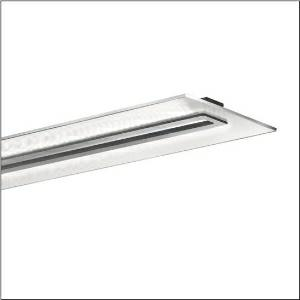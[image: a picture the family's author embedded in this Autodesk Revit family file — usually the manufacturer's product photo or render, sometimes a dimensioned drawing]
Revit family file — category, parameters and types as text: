
# Revit family: vega_r__11_5mn238dlc003_c003
name_source: partatom
category: Lighting Fixtures
units: mm (PartAtom-declared; Revit-internal decimal feet)

## family parameters
Cut with Voids When Loaded = No
Host = Face
Light Source = No
Part Type = Normal
Room Calculation Point = No
Round Connector Dimension = Use Diameter
Shared = No

## types (1)
- --- (1 x LED 3000K / CRI = 80 (unbekannt), 4300 lm, 3000K)
    Apparent Load = 35 VA
    CIE Flux Codes = 61 86 97 62 100
    Color Rendering = 80
    Color Temperature = 3000K
    Default Elevation = 1800 mm
    Description = Vega® 11, office luminaire, primary light control with prismatic reflector, of PMMA, transparent prismatic structure, CAT 2 (L<= 1500cd/m²), light emission: direct/indirect distribution, primary light characteristic: symmetric, installation type: suspended mounting, surface-mounted, LED rated luminous flux: 4.300 lm, light colour: 830, colour temperature: 3000K, control gear: ECG, with terminal, 3+2-pole, max. 2.5mm², mains connection: 230V, AC, 50Hz, connection cable inclusive, cable length: 1,5 m, rated input power: 35W, luminaire housing, rectangular, rounded, of aluminium section, anodised, metallic grey (RAL 9006), length: 1.250 mm, width: 350 mm, height: 43mm, luminaire housing, lower part, of aluminium section, anodised, metallic grey (RAL 9006), of PC, grey, protection rating (complete): IP20, insulation class (complete): insulation class I (protective earthing), certification: CE, standard: EN 50419, packaging unit: 1 piece
    Height = 40 mm  [stored 0.131234 ft]
    Lamp = 1 x LED 3000K / CRI >= 80 (unbekannt)
    Lamp Light Flux = 4300 lm
    Lamp count = 1
    Length = 1250 mm
    Luminous efficacy = 123 lm/W
    Manufacturer = Siteco
    ModVariant = No
    Model = 5MN238DLC003
    Mounting Place = Ceiling
    Mounting Type = Pendant
    Number of Poles = 1
    OnlyDefault = Yes
    Power Factor = 1
    Product Name = Vega® 11
    Product group = office luminaire | ceiling pendant
    ProductGroupID = 905
    Protection Class = Protection class I
    Protection Degree = IP 20
    RLX_Detail_Level = 1
    RlxData = <blob elided: 62757 chars, md5=ca971ff4>
    Socket = socket
    Standby Power = 0 W
    System Light Flux = 4300 lm
    System Power = 35 W
    Type Comments = factory setting: luminous flux: 100 % | dim-lin: 254 | 260 mA
    Type Image = l_1004807.jpg
    URL = http://relux.com
    VarID = @adj_147249
    Voltage = 0 V
    Weight = 0.00 kg
    Width = 350 mm

note: [stored X ft] marks values corroborated as IEEE doubles in the binary element streams (Revit-internal decimal feet)

## geometry (parser evidence)
native form markers: Blend x4, Sweep x10
no freeform markers — native parametric forms only
